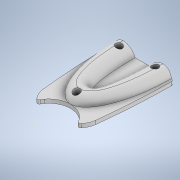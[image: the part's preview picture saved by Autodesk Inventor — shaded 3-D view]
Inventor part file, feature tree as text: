
AUTODESK INVENTOR PART (.ipt)
format: ipt  version: 2021 (Build 250183000, 183)  size: 291,328 bytes
history: native  units: mm
features: sketch x5, extrude x4, fillet x2
ambient origin geometry x8: Origin, YZ Plane, XZ Plane, XY Plane, X Axis, Y Axis, Z Axis, Center Point
bodies: Body1 (feature_tree)
feature tree (11):
  extrude  "Wyciągnięcie proste2"  Depth=3.0mm TaperAngle=0.0deg
  extrude  "Wyciągnięcie proste3"  Depth=7.0mm TaperAngle=0.0deg
  extrude  "Wyciągnięcie proste4"  Depth=5.5mm
  fillet  "Zaokrąglenie1"  Radius=5.5mm
  extrude  "Wyciągnięcie proste5"  Depth=5.5mm
  fillet  "Zaokrąglenie2"  Radius=5.0mm
  sketch  "Szkic11"
  sketch  "Szkic5"
  sketch  "Szkic6"
  sketch  "Szkic7"
  sketch  "Szkic10"
